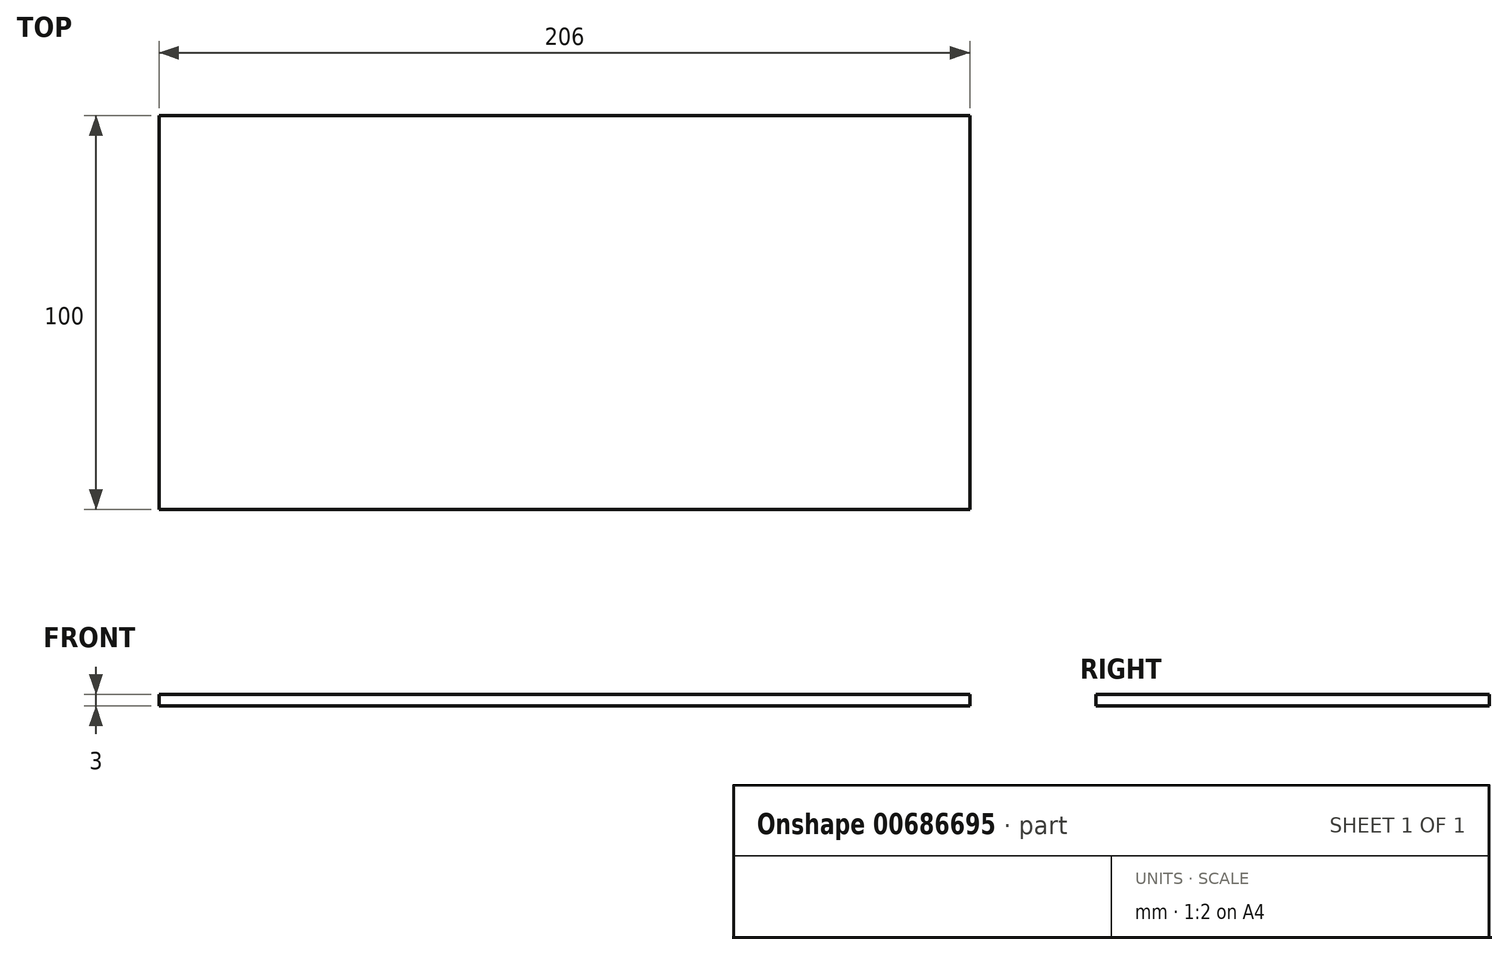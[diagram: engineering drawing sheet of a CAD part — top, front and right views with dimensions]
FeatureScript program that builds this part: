
annotation { "Feature Type Name" : "Feature", "Feature Type Description" : "" }
export const myFeature = defineFeature(function(context is Context, id is Id, definition is map)
    precondition{}
    {
        {
            var Q0;
            Q0=qCreatedBy(makeId("Top.planeOp"),FACE);
            var sketch = newSketch(context, id + "F0", { "sketchPlane" : qUnion([Q0])});
            skLineSegment(sketch, "E0.bottom", {"start": v(0, 0) * mm, "end": v(206, 0) * mm});
            skLineSegment(sketch, "E0.top", {"start": v(0, 100) * mm, "end": v(206, 100) * mm});
            skLineSegment(sketch, "E0.left", {"start": v(0, 0) * mm, "end": v(0, 100) * mm});
            skLineSegment(sketch, "E0.right", {"start": v(206, 0) * mm, "end": v(206, 100) * mm});
            skSolve(sketch);
        }
        {
            var Q0;
            Q0=makeQuery(id+"F0.imprint","IMPRINT",FACE,{"disambiguationData":[TD([[makeQuery(id+"F0.imprint","IMPRINT",EDGE,{"derivedFrom":sQuery(id+"F0.wireOp",EDGE,"E0.bottom")}),1.0]])]});
            extrude(context, id + "F1", {"entities" : qUnion([Q0]), "depth" : 3 * mm, "offsetDistance" : 25 * mm});
        }
    });
